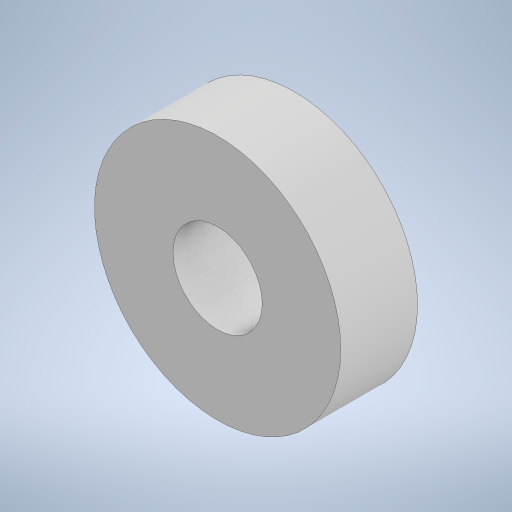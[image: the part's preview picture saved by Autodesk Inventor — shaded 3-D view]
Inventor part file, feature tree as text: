
AUTODESK INVENTOR PART (.ipt)
format: ipt  version: 2023 (Build 270158000, 158)  size: 216,064 bytes
history: native  units: in
note: dims shown in document units (in); Inventor stores cm internally (conversion verified against a paired STEP export)
features: extrude x1, sketch x1
ambient origin geometry x8: Origin, YZ Plane, XZ Plane, XY Plane, X Axis, Y Axis, Z Axis, Center Point
bodies: Solid1 (feature_tree)
feature tree (2):
  extrude  "Extrusion1"  Depth=0.27in
  sketch  "Sketch1"  dims[d0=0.314in d1=0.866in d2=0.27in d3=0.0in]
